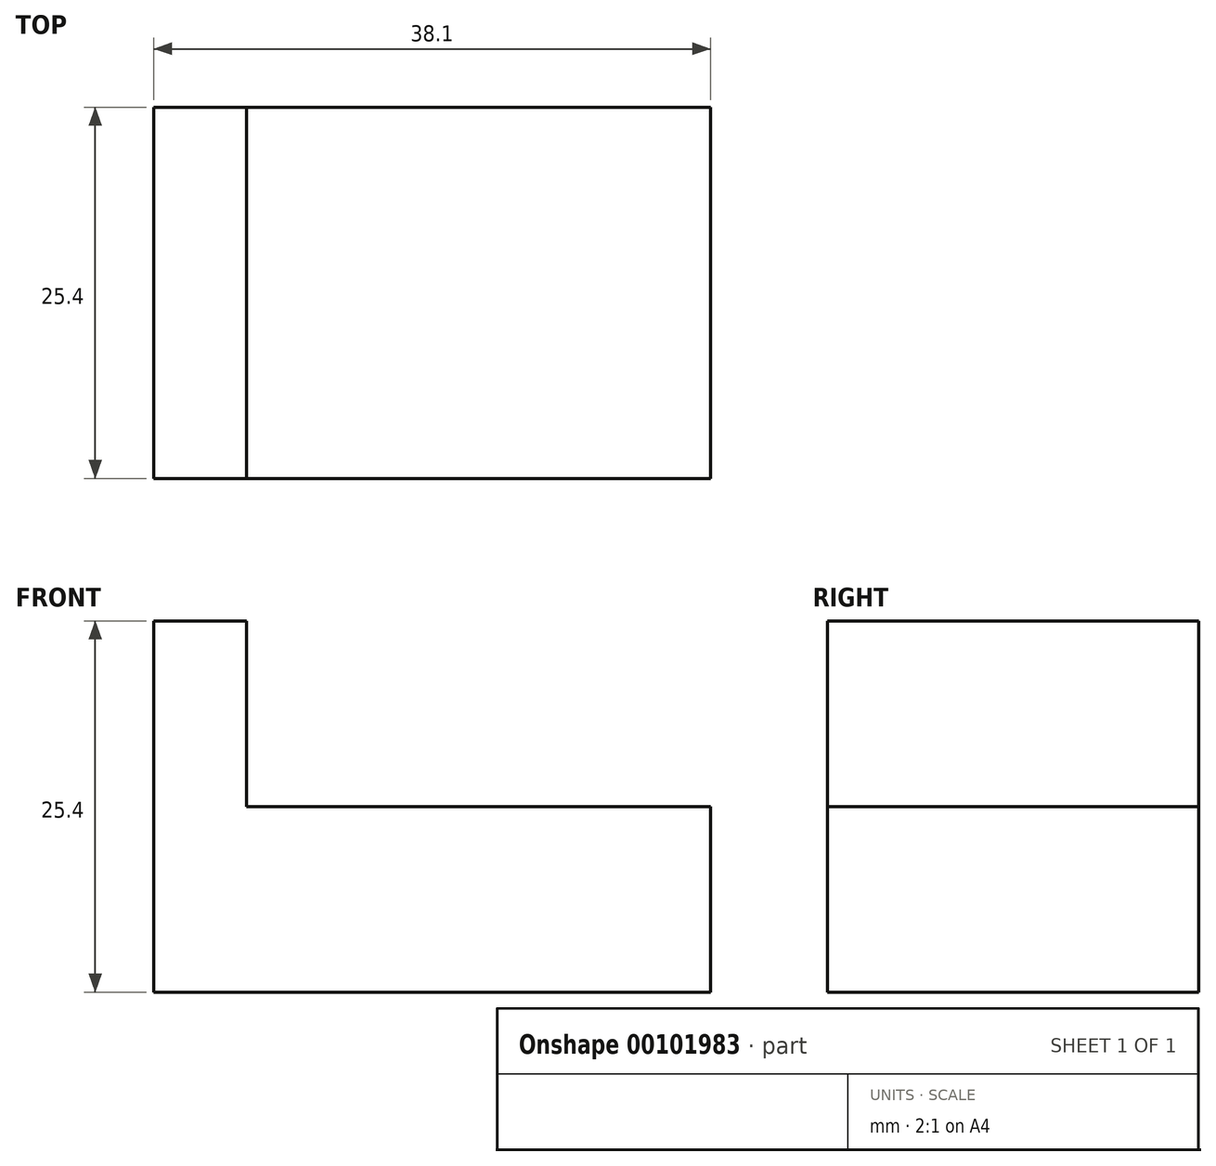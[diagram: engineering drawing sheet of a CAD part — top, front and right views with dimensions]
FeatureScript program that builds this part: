
annotation { "Feature Type Name" : "Feature", "Feature Type Description" : "" }
export const myFeature = defineFeature(function(context is Context, id is Id, definition is map)
    precondition{}
    {
        {
            var Q0;
            Q0=qCreatedBy(makeId("Front.planeOp"),FACE);
            var sketch = newSketch(context, id + "F0", { "sketchPlane" : qUnion([Q0])});
            skLineSegment(sketch, "E0", {"start": v(-28.22, 27.55) * mm, "end": v(-28.22, 2.15) * mm});
            skLineSegment(sketch, "E1", {"start": v(-28.22, 2.15) * mm, "end": v(9.88, 2.15) * mm});
            skLineSegment(sketch, "E2", {"start": v(9.88, 2.15) * mm, "end": v(9.88, 14.85) * mm});
            skLineSegment(sketch, "E3", {"start": v(9.88, 14.85) * mm, "end": v(-21.87, 14.85) * mm});
            skLineSegment(sketch, "E4", {"start": v(-21.87, 14.85) * mm, "end": v(-21.87, 27.55) * mm});
            skLineSegment(sketch, "E5", {"start": v(-21.87, 27.55) * mm, "end": v(-28.22, 27.55) * mm});
            skSolve(sketch);
        }
        {
            var Q0;
            Q0=makeQuery(id+"F0.imprint","IMPRINT",FACE,{"disambiguationData":[TD([[makeQuery(id+"F0.imprint","IMPRINT",EDGE,{"derivedFrom":sQuery(id+"F0.wireOp",EDGE,"E0")}),1.0]])]});
            extrude(context, id + "F1", {"entities" : qUnion([Q0]), "depth" : 25.4 * mm});
        }
    });
